# Revit family: 1
name_source: partatom
category: Pipe Accessories
revit_build: Autodesk Revit 2018 (Build: 20190510_1515(x64)
units: mm (PartAtom-declared; Revit-internal decimal feet)

## family parameters
Always vertical = No
Cut with Voids When Loaded = No
OmniClass Number = 23.65.00.00
OmniClass Title = Supply and Distribution of Liquids and Gases
Part Type = Normal
Round Connector Dimension = Use Diameter
Shared = No
Work Plane-Based = No

## types (1)
- 3/8" Chrome plated
    Antifreeze: = Passiveted Propylene Glycol
    Application fluids = Water or glycol solutions
    BIMobject category = HVAC:Solar Heating
    Brand url = www.pintossi.it
    Conditioning: = as indicated by the producer
    Copper (CU): = < 0,1 mg/kg (< 0,05 mg/kg for steam)
    Description = Pintossi+C SOLAR automatic air vents have the function of automatically eliminating the air that can build up inside a solar heating system.
    Design country = Italy
    Edition number = 0
    Fluid aspect: = Limpid
    IFC Classification = Valve
    Inlet/Outlet Diameter = 10 mm  [stored 0.0328084 ft]
    Iron (FE): = < 0,5 mg/kg (< 0,1 mg/kg for steam)
    Manufacturer = pintossi+C
    Manufacturer country = Italy
    Mass = 0.00 kg
    Masterformat 2014 Code = 23 00 00
    Masterformat 2014 Description = Ventilating, and Air contitioning (HVAC)
    Material Body = Pintossi - Metal - Chrome
    Material Gaskets = Pintossi - Rubber - NBR
    Material Polimer = Pintossi - Plastic - Yellow ABS
    Material main = Brass
    Maximum discharge pressure = 0.0 Pa
    Maximum percentage of glycol [%] = 50
    Maximum working pressure = 600000.0 Pa
    Maximum working temperature = 160 °C
    Model = 507s SOLAR AUTOMATIC AIR VENT
    NBS Reference Code = 55-34-05
    NBS Reference Description = Automatic Air Vents
    OmniClass Code = 23-27 31 00
    OmniClass Description = Valves
    PH: = Between 7 and 8
    Product Guid = 03bc813f-47be-4a76-97fc-87102a4a67a3
    Product SKU = 507s-SOLAR-AUTOMATIC-AIR-VENT
    Product data url = https://www.bimobject.com
    Product family = COMPONENTS-FOR-CENTRAL-HEATING-SYSTEMS
    Product group = AUTOMATIC AIR VENTS
    QR code = https://www.bimobject.com
    UNSPSC Code = 401446
    URL = www.pintossi.it
    Uniclass 1.4 Code = JT10
    Uniclass 1.4 Description = Heating systems
    Uniclass 2.0 Code = PR-55-34-05
    Uniclass 2.0 Description = Automatic Air Vents
    Uniclass 2015 Code = Ss_60
    Uniclass 2015 Name = Heating, cooling and refrigeration systems
    Uniformat II Code = D30
    Uniformat II Description = HVAC

note: [stored X ft] marks values corroborated as IEEE doubles in the binary element streams (Revit-internal decimal feet)

## geometry (parser evidence)
native form markers: Sweep x3
no freeform markers — native parametric forms only
